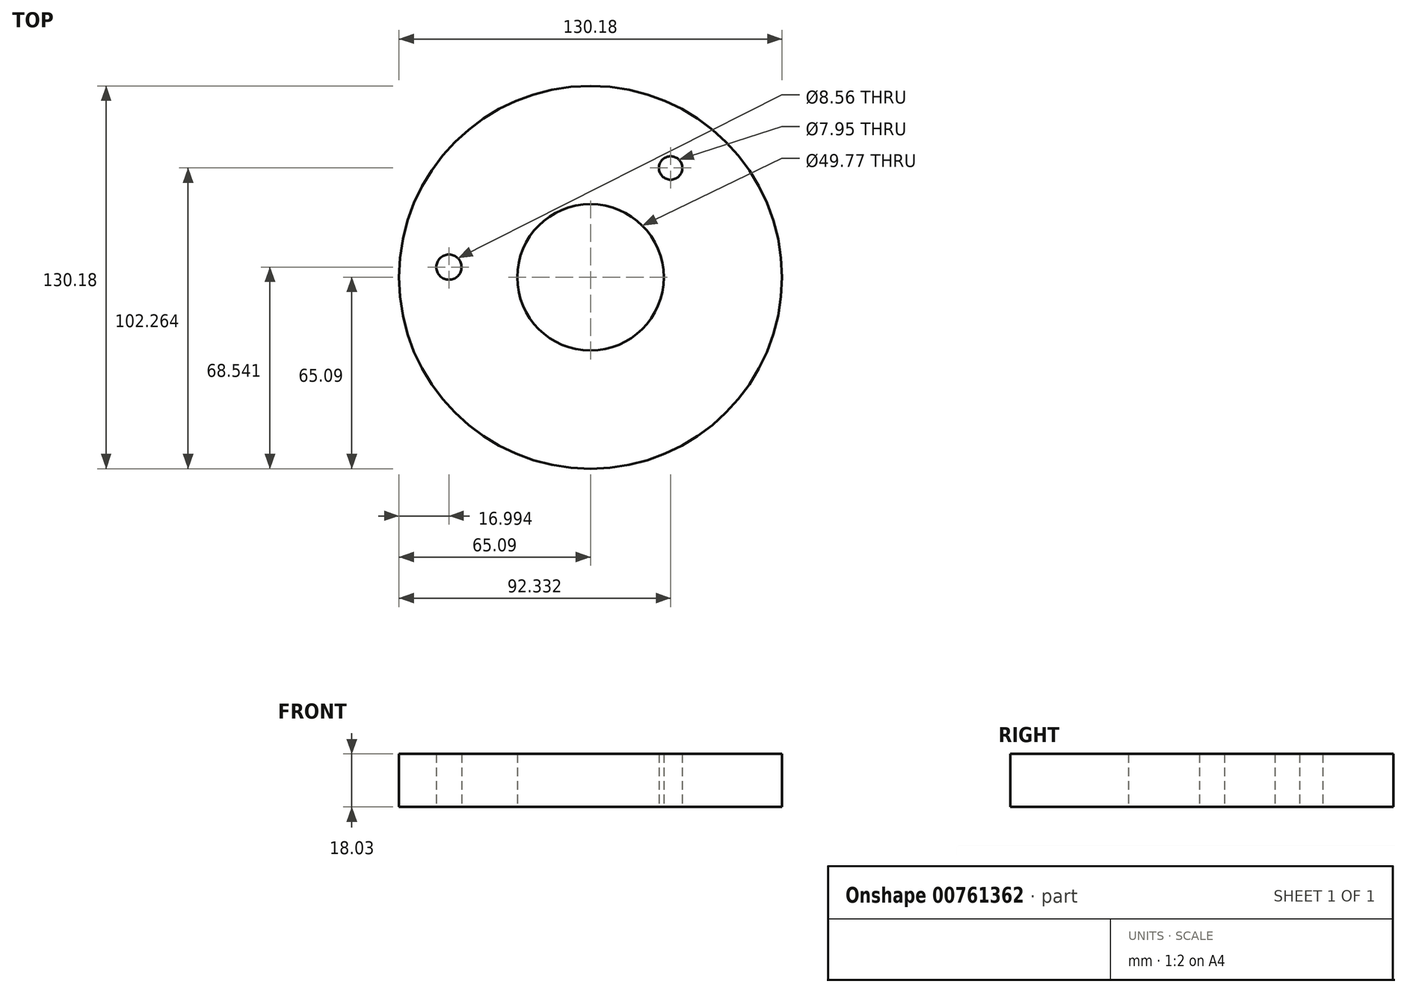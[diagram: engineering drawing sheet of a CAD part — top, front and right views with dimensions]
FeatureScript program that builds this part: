
annotation { "Feature Type Name" : "Feature", "Feature Type Description" : "" }
export const myFeature = defineFeature(function(context is Context, id is Id, definition is map)
    precondition{}
    {
        {
            var Q0;
            Q0=qCreatedBy(makeId("Top.planeOp"),FACE);
            var sketch = newSketch(context, id + "F0", { "sketchPlane" : qUnion([Q0])});
            skCircle(sketch, "E0", {"center": v(0, 0) * mm, "radius": 24.89 * mm});
            skCircle(sketch, "E1", {"center": v(0, 0) * mm, "radius": 65.09 * mm});
            skCircle(sketch, "E2", {"center": v(-48.1, 3.45) * mm, "radius": 4.28 * mm});
            skCircle(sketch, "E3", {"center": v(27.24, 37.17) * mm, "radius": 3.98 * mm});
            skSolve(sketch);
        }
        {
            var Q0;
            Q0=makeQuery(id+"F0.imprint","IMPRINT",FACE,{"disambiguationData":[TD([[makeQuery(id+"F0.imprint","IMPRINT",EDGE,{"derivedFrom":sQuery(id+"F0.wireOp",EDGE,"E0")}),-1.0]])]});
            extrude(context, id + "F1", {"entities" : qUnion([Q0]), "depth" : 18.03 * mm, "offsetDistance" : 25.4 * mm});
        }
    });
